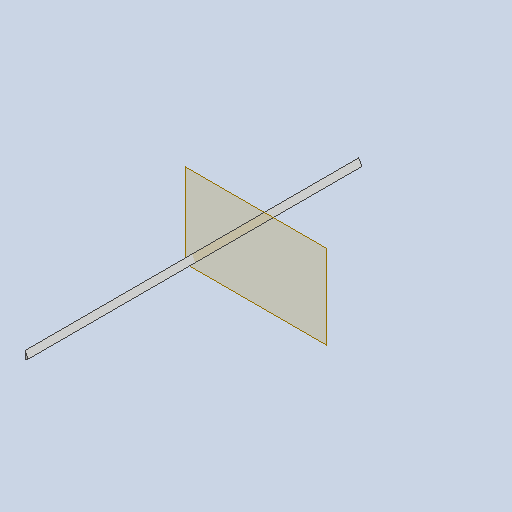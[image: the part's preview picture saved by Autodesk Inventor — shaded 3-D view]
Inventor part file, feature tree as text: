
AUTODESK INVENTOR PART (.ipt)
format: ipt  version: 2023 (Build 270158000, 158)  size: 288,256 bytes
history: native  units: in
note: dims shown in document units (in); Inventor stores cm internally (conversion verified against a paired STEP export)
features: other x9, reference x9, extrude x4, sketch x4, mirror x1, projected_geometry x1
ambient origin geometry x8: Origin, YZ Plane, XZ Plane, XY Plane, X Axis, Y Axis, Z Axis, Center Point
bodies: Body1 (feature_tree)
feature tree (28):
  other  "Bryła1"
  extrude  "Wyciągnięcie proste1"  Depth=3.937in
  extrude  "Wyciągnięcie proste4"  Depth=3.937in TaperAngle=0.0deg
  other  "Płaszczyzna konstrukcyjna1"
  mirror  "Odbij1"
  extrude  "Wyciągnięcie proste5"  Depth=0.0197in
  extrude  "Wyciągnięcie proste6"  Depth=0.0197in
  sketch  "Szkic1"
  reference  "Odniesienie1"
  reference  "Odniesienie2"
  reference  "Odniesienie3"
  reference  "Odniesienie4"
  sketch  "Szkic5"
  reference  "Odniesienie15"
  reference  "Odniesienie16"
  reference  "Odniesienie17"
  sketch  "Szkic6"
  reference  "Odniesienie18"
  reference  "Odniesienie19"
  sketch  "Szkic7"
  projected_geometry  "Pętla rzutowana3"
  other  "<userpath>\Desktop\MojeRoboty\Stefan\mechanics 2\STEFAN.iam"
  other  "STEFAN.iam"
  other  "podstawa:1"
  other  "koło_minisumo:2"
  other  "plug_nowy:1"
  other  "mocowanie sharpow:1"
  other  "plug_2:1"
